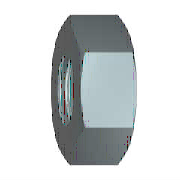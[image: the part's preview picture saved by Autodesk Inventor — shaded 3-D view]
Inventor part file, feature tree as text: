
AUTODESK INVENTOR PART (.ipt)
format: ipt  version: 2022 (Build 260153000, 153)  size: 175,104 bytes
history: native  units: mm (DEFAULTED — no unit token found)
features: sketch x3, chamfer x1, hole x1, other x1, plane x1
ambient origin geometry x7: Origin, YZ Plane, XZ Plane, X Axis, Y Axis, Z Axis, Center Point
bodies: Solid1 (feature_tree), Body (feature_tree)
feature tree (7):
  chamfer  "Chamfer1"  Angle=30.0deg  [1 undecoded]
  hole  "Thread"  [1 undecoded]
  other  "Work Axis1"
  plane  "Work Plane1"
  sketch  "Sketch1"  dims[d0=8.082904mm]
  sketch  "Sketch2"  dims[d1=2.4mm]
  sketch  "Sketch3"  dims[d2=0.0mm d3=30.0deg d4=30.0deg d5=7.0mm d6=7.0mm d7=90.0deg d25=3.242mm d26=6.0mm d27=4.0mm d28=2.0mm d29=14.3117mm d30=8.0mm d31=20.594885mm d8=0.378886mm d9=30.0deg d10=0.378886mm d11=30.0deg d13=0.0mm d14=0.0mm d39=0.0mm d40=0.378886mm d41=0.378886mm d42=0.0mm]
note: 2 required parameter values undecoded (feature->parameter linkage not recoverable at this tier; creation-order binding heuristic only, values carry confidence <= 0.55)
